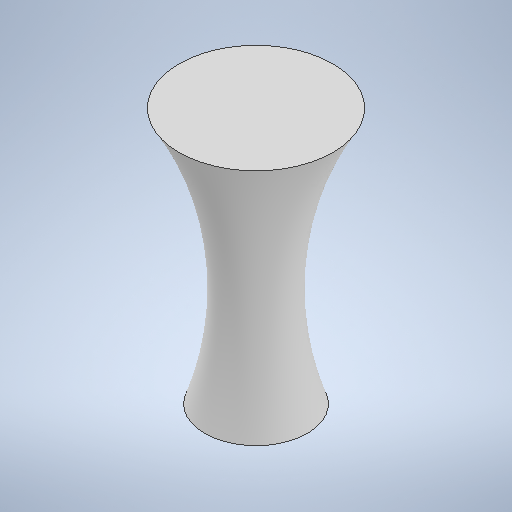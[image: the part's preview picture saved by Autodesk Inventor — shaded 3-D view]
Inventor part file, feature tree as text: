
AUTODESK INVENTOR PART (.ipt)
format: ipt  version: 2025.3 (Build 293356000, 356)  size: 276,480 bytes
history: native  units: in
note: dims shown in document units (in); Inventor stores cm internally (conversion verified against a paired STEP export)
features: revolve x1, sketch x1
ambient origin geometry x8: Origin, YZ Plane, XZ Plane, XY Plane, X Axis, Y Axis, Z Axis, Center Point
bodies: Solid1 (feature_tree)
feature tree (2):
  revolve  "Revolution1"  [1 undecoded]
  sketch  "Sketch1"  dims[d0=15.748in d1=39.3701in d2=23.622in d3=47.2441in d4=90.0deg]
note: 1 required parameter value undecoded (feature->parameter linkage not recoverable at this tier; creation-order binding heuristic only, values carry confidence <= 0.55)
